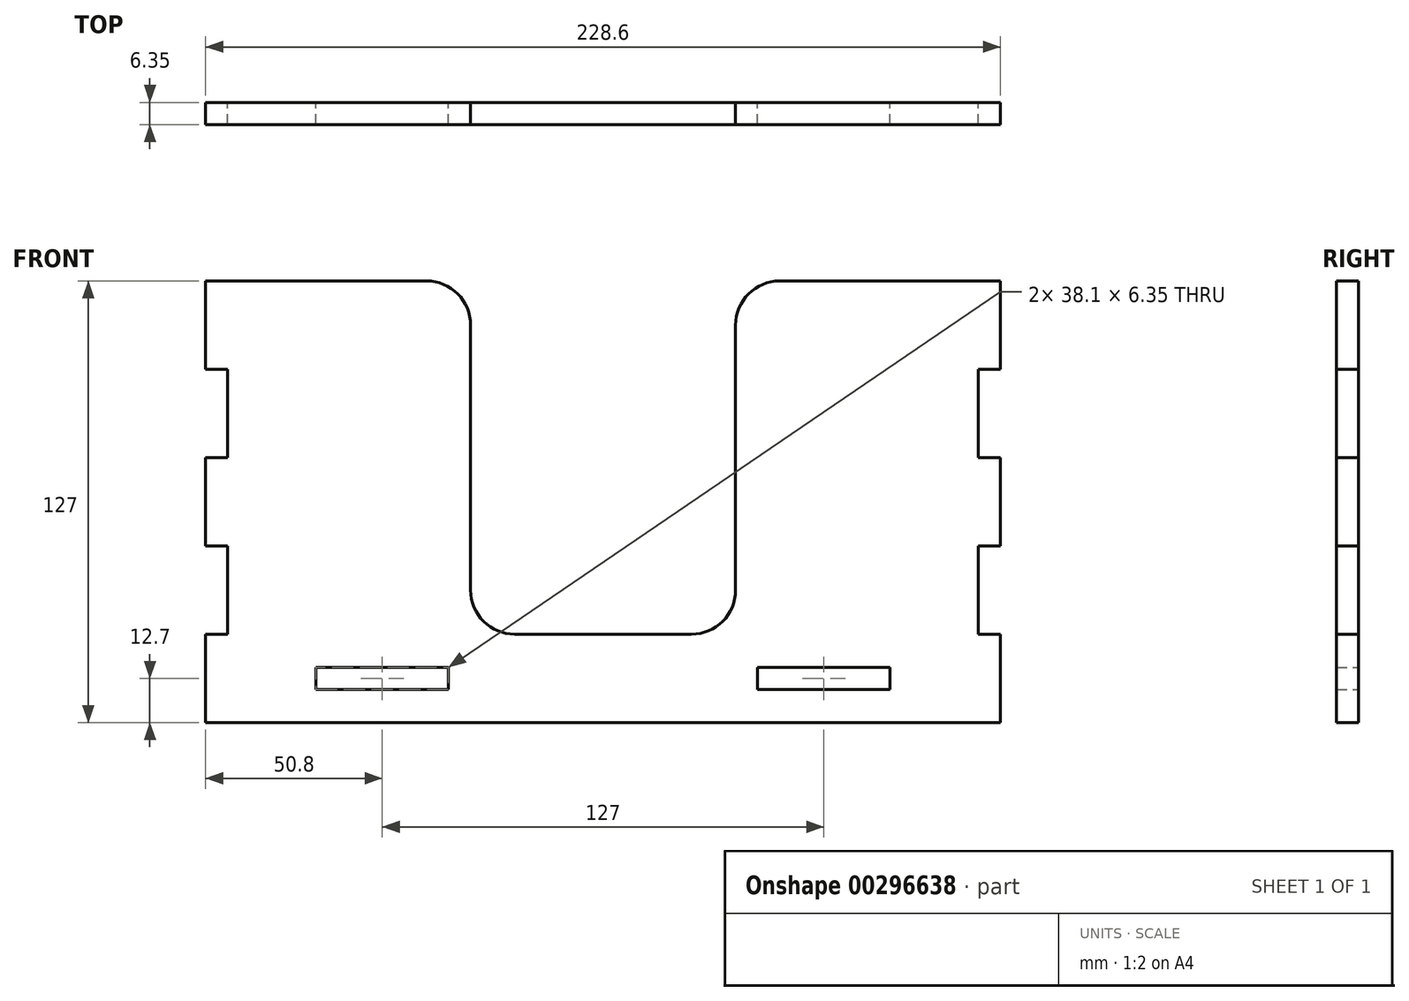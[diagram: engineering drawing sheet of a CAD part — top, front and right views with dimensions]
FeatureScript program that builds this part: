
annotation { "Feature Type Name" : "Feature", "Feature Type Description" : "" }
export const myFeature = defineFeature(function(context is Context, id is Id, definition is map)
    precondition{}
    {
        {
            var Q0;
            Q0=qCreatedBy(makeId("Front.planeOp"),FACE);
            var sketch = newSketch(context, id + "F0", { "sketchPlane" : qUnion([Q0])});
            skLineSegment(sketch, "E0.bottom", {"start": v(114.3, -12.7) * mm, "end": v(-114.3, -12.7) * mm});
            skLineSegment(sketch, "E0.top", {"start": v(114.3, 114.3) * mm, "end": v(50.8, 114.3) * mm});
            skLineSegment(sketch, "E0.left", {"start": v(114.3, -12.7) * mm, "end": v(114.3, 12.7) * mm});
            skLineSegment(sketch, "E0.right", {"start": v(-114.3, -12.7) * mm, "end": v(-114.3, 12.7) * mm});
            skPoint(sketch, "E0.middle", {"position": v(0, 50.8) * mm});
            skLineSegment(sketch, "E1.top", {"start": v(-25.4, 12.7) * mm, "end": v(25.4, 12.7) * mm});
            skLineSegment(sketch, "E1.left", {"start": v(-38.1, 101.6) * mm, "end": v(-38.1, 25.4) * mm});
            skLineSegment(sketch, "E1.right", {"start": v(38.1, 101.6) * mm, "end": v(38.1, 25.4) * mm});
            skLineSegment(sketch, "E2.trimOffspring", {"start": v(-50.8, 114.3) * mm, "end": v(-114.3, 114.3) * mm});
            skLineSegment(sketch, "E3", {"start": v(0, 12.7) * mm, "end": v(0, 0) * mm, "construction": true});
            skLineSegment(sketch, "E4.bottom", {"start": v(-82.55, 3.17) * mm, "end": v(-44.45, 3.17) * mm});
            skLineSegment(sketch, "E4.top", {"start": v(-82.55, -3.17) * mm, "end": v(-44.45, -3.17) * mm});
            skLineSegment(sketch, "E4.left", {"start": v(-82.55, 3.17) * mm, "end": v(-82.55, -3.18) * mm});
            skLineSegment(sketch, "E4.right", {"start": v(-44.45, 3.17) * mm, "end": v(-44.45, -3.17) * mm});
            skLineSegment(sketch, "E5.bottom", {"start": v(-114.3, 88.9) * mm, "end": v(-107.95, 88.9) * mm});
            skLineSegment(sketch, "E5.top", {"start": v(-114.3, 63.5) * mm, "end": v(-107.95, 63.5) * mm});
            skLineSegment(sketch, "E5.right", {"start": v(-107.95, 88.9) * mm, "end": v(-107.95, 63.5) * mm});
            skLineSegment(sketch, "E6.bottom", {"start": v(-114.3, 38.1) * mm, "end": v(-107.95, 38.1) * mm});
            skLineSegment(sketch, "E6.top", {"start": v(-114.3, 12.7) * mm, "end": v(-107.95, 12.7) * mm});
            skLineSegment(sketch, "E6.right", {"start": v(-107.95, 38.1) * mm, "end": v(-107.95, 12.7) * mm});
            skPoint(sketch, "E7", {"position": v(-63.5, 0) * mm});
            skPoint(sketch, "E7.positionSnap0", {"position": v(-44.45, 0) * mm});
            skPoint(sketch, "E7.positionSnap1", {"position": v(-63.5, -3.17) * mm});
            skLineSegment(sketch, "E8", {"start": v(-63.5, 0) * mm, "end": v(0, 0) * mm, "construction": true});
            skLineSegment(sketch, "E9.trimOffspring", {"start": v(-114.3, 88.9) * mm, "end": v(-114.3, 114.3) * mm});
            skLineSegment(sketch, "E10.trimOffspring", {"start": v(-114.3, 38.1) * mm, "end": v(-114.3, 63.5) * mm});
            skLineSegment(sketch, "E11.MirrorCS", {"start": v(114.3, 38.1) * mm, "end": v(107.95, 38.1) * mm});
            skLineSegment(sketch, "E12.MirrorCS", {"start": v(114.3, 88.9) * mm, "end": v(107.95, 88.9) * mm});
            skLineSegment(sketch, "E13.MirrorCS", {"start": v(114.3, 12.7) * mm, "end": v(107.95, 12.7) * mm});
            skLineSegment(sketch, "E14.MirrorCS", {"start": v(114.3, 63.5) * mm, "end": v(107.95, 63.5) * mm});
            skLineSegment(sketch, "E15.MirrorCS", {"start": v(114.3, 38.1) * mm, "end": v(114.3, 63.5) * mm});
            skLineSegment(sketch, "E16.MirrorCS", {"start": v(107.95, 38.1) * mm, "end": v(107.95, 12.7) * mm});
            skLineSegment(sketch, "E17.MirrorCS", {"start": v(107.95, 88.9) * mm, "end": v(107.95, 63.5) * mm});
            skPoint(sketch, "E18.MirrorP", {"position": v(63.5, 0) * mm});
            skLineSegment(sketch, "E19.MirrorCS", {"start": v(44.45, 3.17) * mm, "end": v(44.45, -3.17) * mm});
            skLineSegment(sketch, "E20.MirrorCS", {"start": v(82.55, 3.17) * mm, "end": v(82.55, -3.18) * mm});
            skLineSegment(sketch, "E21.MirrorCS", {"start": v(82.55, -3.17) * mm, "end": v(44.45, -3.17) * mm});
            skLineSegment(sketch, "E22.MirrorCS", {"start": v(82.55, 3.17) * mm, "end": v(44.45, 3.17) * mm});
            skPoint(sketch, "E23.MirrorP", {"position": v(44.45, 0) * mm});
            skPoint(sketch, "E24.MirrorP", {"position": v(63.5, -3.17) * mm});
            skLineSegment(sketch, "E25.trimOffspring", {"start": v(114.3, 88.9) * mm, "end": v(114.3, 114.3) * mm});
            skPoint(sketch, "E26.visualSharp", {"position": v(-38.1, 114.3) * mm});
            skArc(sketch, "E26.filletArc", {"start": v(-38.1, 101.6) * mm, "mid": v(-41.82, 110.58) * mm, "end": v(-50.8, 114.3) * mm});
            skPoint(sketch, "E27.visualSharp", {"position": v(-38.1, 12.7) * mm});
            skArc(sketch, "E27.filletArc", {"start": v(-38.1, 25.4) * mm, "mid": v(-34.38, 16.42) * mm, "end": v(-25.4, 12.7) * mm});
            skPoint(sketch, "E28.visualSharp", {"position": v(38.1, 12.7) * mm});
            skArc(sketch, "E28.filletArc", {"start": v(25.4, 12.7) * mm, "mid": v(34.38, 16.42) * mm, "end": v(38.1, 25.4) * mm});
            skPoint(sketch, "E29.visualSharp", {"position": v(38.1, 114.3) * mm});
            skArc(sketch, "E29.filletArc", {"start": v(50.8, 114.3) * mm, "mid": v(41.82, 110.58) * mm, "end": v(38.1, 101.6) * mm});
            skSolve(sketch);
        }
        {
            var Q0;
            Q0 = qSketchRegion(id + "F0", true);
            extrude(context, id + "F1", {"entities" : qUnion([Q0]), "depth" : 6.35 * mm});
        }
    });
